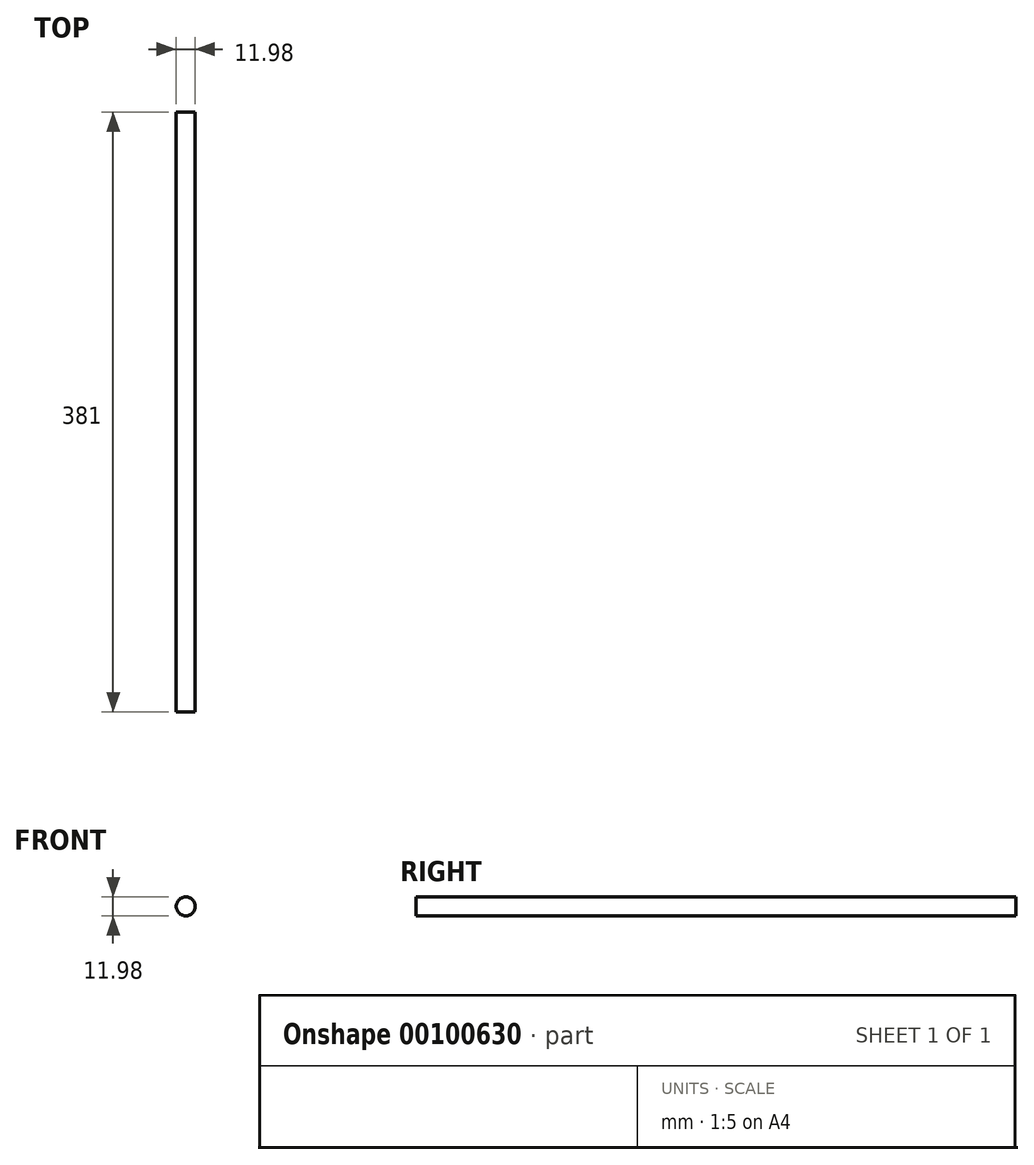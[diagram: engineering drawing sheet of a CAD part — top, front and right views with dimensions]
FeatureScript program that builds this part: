
annotation { "Feature Type Name" : "Feature", "Feature Type Description" : "" }
export const myFeature = defineFeature(function(context is Context, id is Id, definition is map)
    precondition{}
    {
        {
            var Q0;
            Q0=qCreatedBy(makeId("Front.planeOp"),FACE);
            var sketch = newSketch(context, id + "F0", { "sketchPlane" : qUnion([Q0])});
            skCircle(sketch, "E0", {"center": v(0, 0) * mm, "radius": 6 * mm});
            skSolve(sketch);
        }
        {
            var Q0;
            Q0=makeQuery(id+"F0.imprint","IMPRINT",FACE,{"disambiguationData":[TD([[makeQuery(id+"F0.imprint","IMPRINT",EDGE,{"derivedFrom":sQuery(id+"F0.wireOp",EDGE,"E0")}),1.0]])]});
            extrude(context, id + "F1", {"entities" : qUnion([Q0]), "depth" : 381 * mm});
        }
    });
